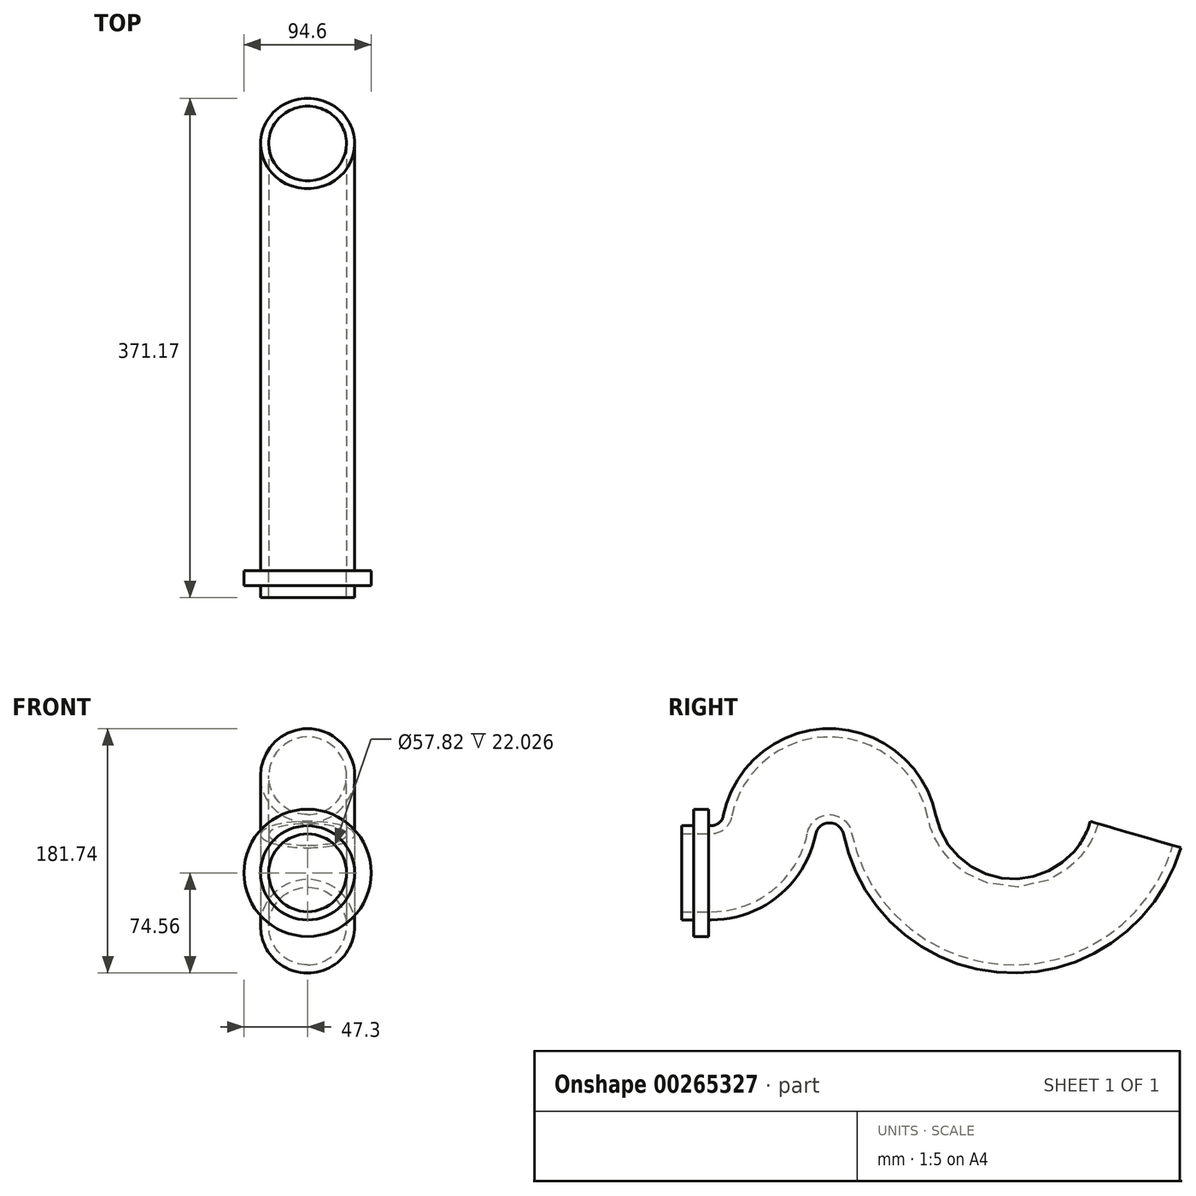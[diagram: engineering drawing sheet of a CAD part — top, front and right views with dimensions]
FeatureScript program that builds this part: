
annotation { "Feature Type Name" : "Feature", "Feature Type Description" : "" }
export const myFeature = defineFeature(function(context is Context, id is Id, definition is map)
    precondition{}
    {
        {
            var Q0;
            Q0=qCreatedBy(makeId("Front.planeOp"),FACE);
            var sketch = newSketch(context, id + "F0", { "sketchPlane" : qUnion([Q0])});
            skCircle(sketch, "E0", {"center": v(0, 0) * mm, "radius": 35 * mm});
            skCircle(sketch, "E1", {"center": v(0, 0) * mm, "radius": 28.91 * mm});
            skSolve(sketch);
        }
        {
            var Q0;
            Q0=qCreatedBy(makeId("Right.planeOp"),FACE);
            var sketch = newSketch(context, id + "F1", { "sketchPlane" : qUnion([Q0])});
            skLineSegment(sketch, "E2.0", {"start": v(0, -35) * mm, "end": v(0, 35) * mm});
            skLineSegment(sketch, "E3", {"start": v(0, 0) * mm, "end": v(22.03, 0) * mm});
            skArc(sketch, "E4", {"start": v(22.03, 0) * mm, "mid": v(50.07, 10.03) * mm, "end": v(65.39, 35.56) * mm});
            skArc(sketch, "E5", {"start": v(65.39, 35.56) * mm, "mid": v(109.92, 72.18) * mm, "end": v(154.64, 35.8) * mm});
            skArc(sketch, "E6", {"start": v(154.64, 35.8) * mm, "mid": v(243.23, -39.49) * mm, "end": v(337.56, 28.45) * mm});
            skSolve(sketch);
        }
        {
            var Q0;
            Q0=makeQuery(id+"F0.imprint","IMPRINT",FACE,{"disambiguationData":[TD([[makeQuery(id+"F0.imprint","IMPRINT",EDGE,{"derivedFrom":sQuery(id+"F0.wireOp",EDGE,"E0")}),1.0]])]});
            var Q1;
            Q1=sQuery(id+"F1.wireOp",EDGE,"E3");
            var Q2;
            Q2=sQuery(id+"F1.wireOp",EDGE,"E4");
            var Q3;
            Q3=sQuery(id+"F1.wireOp",EDGE,"E5");
            var Q4;
            Q4=sQuery(id+"F1.wireOp",EDGE,"E6");
            sweep(context, id + "F2", {"profiles" : qUnion([Q0]), "path" : qUnion([Q1, Q2, Q3, Q4])});
        }
        {
            var Q0;
            Q0=qCreatedBy(makeId("Front.planeOp"),FACE);
            cPlane(context, id + "F3", {"entities" : qUnion([Q0]), "cplaneType" : CPlaneType.OFFSET, "offset" : 9 * mm, "oppositeDirection" : true, "width" : 150 * mm, "height" : 150 * mm});
        }
        {
            var Q0;
            Q0=qCreatedBy(id+"F3.planeOp",FACE);
            var sketch = newSketch(context, id + "F4", { "sketchPlane" : qUnion([Q0])});
            skCircle(sketch, "E7", {"center": v(0, 0) * mm, "radius": 47.3 * mm});
            skCircle(sketch, "E8.0", {"center": v(0, 0) * mm, "radius": 35 * mm});
            skSolve(sketch);
        }
        {
            var Q0;
            Q0=makeQuery(id+"F4.imprint","IMPRINT",FACE,{"disambiguationData":[TD([[makeQuery(id+"F4.imprint","IMPRINT",EDGE,{"derivedFrom":sQuery(id+"F4.wireOp",EDGE,"E7")}),1.0]])]});
            extrude(context, id + "F5", {"entities" : qUnion([Q0]), "operationType" : NewBodyOperationType.ADD, "oppositeDirection" : true, "depth" : 11 * mm});
        }
    });
